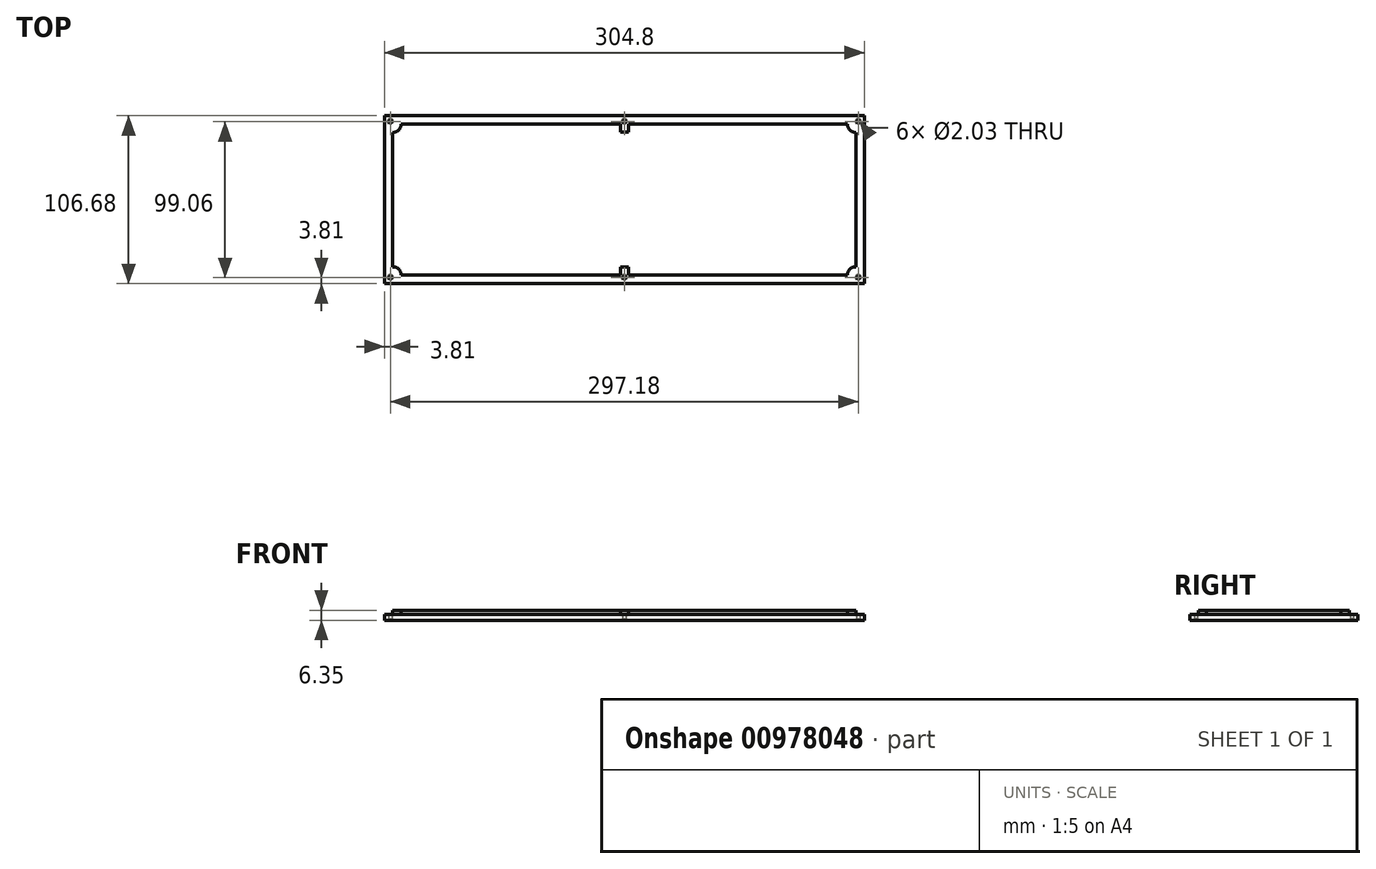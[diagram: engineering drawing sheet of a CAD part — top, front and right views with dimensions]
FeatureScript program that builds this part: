
annotation { "Feature Type Name" : "Feature", "Feature Type Description" : "" }
export const myFeature = defineFeature(function(context is Context, id is Id, definition is map)
    precondition{}
    {
        {
            var Q0;
            Q0=qCreatedBy(makeId("Top.planeOp"),FACE);
            var sketch = newSketch(context, id + "F0", { "sketchPlane" : qUnion([Q0])});
            skLineSegment(sketch, "E0.bottom", {"start": v(0, 0) * mm, "end": v(304.8, 0) * mm});
            skLineSegment(sketch, "E0.top", {"start": v(0, -106.68) * mm, "end": v(304.8, -106.68) * mm});
            skLineSegment(sketch, "E0.left", {"start": v(0, 0) * mm, "end": v(0, -106.68) * mm});
            skLineSegment(sketch, "E0.right", {"start": v(304.8, 0) * mm, "end": v(304.8, -106.68) * mm});
            skSolve(sketch);
        }
        {
            var Q0;
            Q0=makeQuery(id+"F0.imprint","IMPRINT",FACE,{"disambiguationData":[TD([[makeQuery(id+"F0.imprint","IMPRINT",EDGE,{"derivedFrom":sQuery(id+"F0.wireOp",EDGE,"E0.bottom")}),-1.0]])]});
            extrude(context, id + "F1", {"entities" : qUnion([Q0]), "depth" : 3.8 * mm, "offsetDistance" : 25.4 * mm});
        }
        {
            var Q0;
            Q0=makeQuery(id+"F1.opExtrude","CAP_FACE",FACE,{"disambiguationData":[OSD([sQuery(id+"F0.wireOp",EDGE,"E0.bottom"),sQuery(id+"F0.wireOp",EDGE,"E0.top"),sQuery(id+"F0.wireOp",EDGE,"E0.left"),sQuery(id+"F0.wireOp",EDGE,"E0.right")])],"isStart":false});
            var sketch = newSketch(context, id + "F2", { "sketchPlane" : qUnion([Q0])});
            skLineSegment(sketch, "E1.bottom", {"start": v(5.33, -5.33) * mm, "end": v(299.47, -5.33) * mm});
            skLineSegment(sketch, "E1.top", {"start": v(5.33, -101.35) * mm, "end": v(299.47, -101.35) * mm});
            skLineSegment(sketch, "E1.left", {"start": v(5.33, -5.33) * mm, "end": v(5.33, -101.35) * mm});
            skLineSegment(sketch, "E1.right", {"start": v(299.47, -5.33) * mm, "end": v(299.47, -101.35) * mm});
            skSolve(sketch);
        }
        {
            var Q0;
            Q0 = qSketchRegion(id + "F2", true);
            extrude(context, id + "F3", {"entities" : qUnion([Q0]), "operationType" : NewBodyOperationType.ADD, "depth" : 2.54 * mm, "offsetDistance" : 25.4 * mm});
        }
        {
            var Q0;
            Q0=makeQuery(id+"F3.opExtrude","CAP_FACE",FACE,{"disambiguationData":[OSD([sQuery(id+"F2.wireOp",EDGE,"E1.bottom"),sQuery(id+"F2.wireOp",EDGE,"E1.top"),sQuery(id+"F2.wireOp",EDGE,"E1.left"),sQuery(id+"F2.wireOp",EDGE,"E1.right")])],"isStart":false});
            var sketch = newSketch(context, id + "F4", { "sketchPlane" : qUnion([Q0])});
            skLineSegment(sketch, "E2.bottom", {"start": v(5.33, -5.33) * mm, "end": v(10.67, -5.33) * mm});
            skLineSegment(sketch, "E2.top", {"start": v(5.33, -10.67) * mm, "end": v(10.67, -10.67) * mm});
            skLineSegment(sketch, "E2.left", {"start": v(5.33, -5.33) * mm, "end": v(5.33, -10.67) * mm});
            skLineSegment(sketch, "E2.right", {"start": v(10.67, -5.33) * mm, "end": v(10.67, -10.67) * mm});
            skLineSegment(sketch, "E3.bottom", {"start": v(5.33, -101.35) * mm, "end": v(10.67, -101.35) * mm});
            skLineSegment(sketch, "E3.top", {"start": v(5.33, -96.01) * mm, "end": v(10.67, -96.01) * mm});
            skLineSegment(sketch, "E3.left", {"start": v(5.33, -101.35) * mm, "end": v(5.33, -96.01) * mm});
            skLineSegment(sketch, "E3.right", {"start": v(10.67, -101.35) * mm, "end": v(10.67, -96.01) * mm});
            skLineSegment(sketch, "E4.bottom", {"start": v(299.47, -5.33) * mm, "end": v(294.13, -5.33) * mm});
            skLineSegment(sketch, "E4.top", {"start": v(299.47, -10.67) * mm, "end": v(294.13, -10.67) * mm});
            skLineSegment(sketch, "E4.left", {"start": v(299.47, -5.33) * mm, "end": v(299.47, -10.67) * mm});
            skLineSegment(sketch, "E4.right", {"start": v(294.13, -5.33) * mm, "end": v(294.13, -10.67) * mm});
            skLineSegment(sketch, "E5.bottom", {"start": v(299.47, -101.35) * mm, "end": v(294.13, -101.35) * mm});
            skLineSegment(sketch, "E5.top", {"start": v(299.47, -96.01) * mm, "end": v(294.13, -96.01) * mm});
            skLineSegment(sketch, "E5.left", {"start": v(299.47, -101.35) * mm, "end": v(299.47, -96.01) * mm});
            skLineSegment(sketch, "E5.right", {"start": v(294.13, -101.35) * mm, "end": v(294.13, -96.01) * mm});
            skLineSegment(sketch, "E6.bottom", {"start": v(149.86, -5.33) * mm, "end": v(154.94, -5.33) * mm});
            skLineSegment(sketch, "E6.top", {"start": v(149.86, -10.41) * mm, "end": v(154.94, -10.41) * mm});
            skLineSegment(sketch, "E6.left", {"start": v(149.86, -5.33) * mm, "end": v(149.86, -10.41) * mm});
            skLineSegment(sketch, "E6.right", {"start": v(154.94, -5.33) * mm, "end": v(154.94, -10.41) * mm});
            skLineSegment(sketch, "E7.bottom", {"start": v(149.86, -101.35) * mm, "end": v(154.94, -101.35) * mm});
            skLineSegment(sketch, "E7.top", {"start": v(149.86, -96.27) * mm, "end": v(154.94, -96.27) * mm});
            skLineSegment(sketch, "E7.left", {"start": v(149.86, -101.35) * mm, "end": v(149.86, -96.27) * mm});
            skLineSegment(sketch, "E7.right", {"start": v(154.94, -101.35) * mm, "end": v(154.94, -96.27) * mm});
            skSolve(sketch);
        }
        {
            var Q0;
            Q0 = qSketchRegion(id + "F4", true);
            extrude(context, id + "F5", {"entities" : qUnion([Q0]), "operationType" : NewBodyOperationType.ADD, "depth" : 25.4 * mm, "offsetDistance" : 25.4 * mm});
        }
        {
            var Q0;
            Q0=makeQuery(id+"F5.opExtrude","SWEPT_EDGE",EDGE,{"disambiguationData":[OSD([sQuery(id+"F4.wireOp",EDGE,"E5.top"),sQuery(id+"F4.wireOp",EDGE,"E5.right")])]});
            var Q1;
            Q1=makeQuery(id+"F5.opExtrude","SWEPT_EDGE",EDGE,{"disambiguationData":[OSD([sQuery(id+"F4.wireOp",EDGE,"E4.top"),sQuery(id+"F4.wireOp",EDGE,"E4.right")])]});
            var Q2;
            Q2=makeQuery(id+"F5.opExtrude","SWEPT_EDGE",EDGE,{"disambiguationData":[OSD([sQuery(id+"F4.wireOp",EDGE,"E2.top"),sQuery(id+"F4.wireOp",EDGE,"E2.right")])]});
            var Q3;
            Q3=makeQuery(id+"F5.opExtrude","SWEPT_EDGE",EDGE,{"disambiguationData":[OSD([sQuery(id+"F4.wireOp",EDGE,"E3.top"),sQuery(id+"F4.wireOp",EDGE,"E3.right")])]});
            fillet(context, id + "F6", {"entities" : qUnion([Q0, Q1, Q2, Q3]), "tangentPropagation" : true, "radius" : 5.08 * mm, "defaultsChanged" : false, "vertexSettings" : [], "allowEdgeOverflow" : false});
        }
        {
            var Q0;
            Q0=makeQuery(id+"F5.opExtrude","CAP_FACE",FACE,{"disambiguationData":[OSD([sQuery(id+"F4.wireOp",EDGE,"E2.bottom"),sQuery(id+"F4.wireOp",EDGE,"E2.top"),sQuery(id+"F4.wireOp",EDGE,"E2.left"),sQuery(id+"F4.wireOp",EDGE,"E2.right")])],"isStart":false});
            var Q1;
            Q1=makeQuery(id+"F5.opExtrude","CAP_FACE",FACE,{"disambiguationData":[OSD([sQuery(id+"F4.wireOp",EDGE,"E3.bottom"),sQuery(id+"F4.wireOp",EDGE,"E3.top"),sQuery(id+"F4.wireOp",EDGE,"E3.left"),sQuery(id+"F4.wireOp",EDGE,"E3.right")])],"isStart":false});
            var Q2;
            Q2=makeQuery(id+"F5.opExtrude","CAP_FACE",FACE,{"disambiguationData":[OSD([sQuery(id+"F4.wireOp",EDGE,"E4.bottom"),sQuery(id+"F4.wireOp",EDGE,"E4.top"),sQuery(id+"F4.wireOp",EDGE,"E4.left"),sQuery(id+"F4.wireOp",EDGE,"E4.right")])],"isStart":false});
            var Q3;
            Q3=makeQuery(id+"F5.opExtrude","CAP_FACE",FACE,{"disambiguationData":[OSD([sQuery(id+"F4.wireOp",EDGE,"E5.bottom"),sQuery(id+"F4.wireOp",EDGE,"E5.top"),sQuery(id+"F4.wireOp",EDGE,"E5.left"),sQuery(id+"F4.wireOp",EDGE,"E5.right")])],"isStart":false});
            extrude(context, id + "F7", {"entities" : qUnion([Q0, Q1, Q2, Q3]), "operationType" : NewBodyOperationType.REMOVE, "oppositeDirection" : true, "depth" : 27.94 * mm, "offsetDistance" : 25.4 * mm});
        }
        {
            var Q0;
            Q0=makeQuery(id+"F1.opExtrude","CAP_FACE",FACE,{"disambiguationData":[OSD([sQuery(id+"F0.wireOp",EDGE,"E0.bottom"),sQuery(id+"F0.wireOp",EDGE,"E0.top"),sQuery(id+"F0.wireOp",EDGE,"E0.left"),sQuery(id+"F0.wireOp",EDGE,"E0.right")])],"isStart":true});
            var sketch = newSketch(context, id + "F8", { "sketchPlane" : qUnion([Q0])});
            skLineSegment(sketch, "E8.bottom", {"start": v(0, 106.68) * mm, "end": v(3.8, 106.68) * mm});
            skLineSegment(sketch, "E8.top", {"start": v(0, 102.87) * mm, "end": v(3.8, 102.87) * mm});
            skLineSegment(sketch, "E8.left", {"start": v(0, 106.68) * mm, "end": v(0, 102.87) * mm});
            skLineSegment(sketch, "E8.right", {"start": v(3.81, 106.68) * mm, "end": v(3.81, 102.87) * mm});
            skLineSegment(sketch, "E9.bottom", {"start": v(0, 0) * mm, "end": v(3.8, 0) * mm});
            skLineSegment(sketch, "E9.top", {"start": v(0, 3.81) * mm, "end": v(3.8, 3.81) * mm});
            skLineSegment(sketch, "E9.left", {"start": v(0, 0) * mm, "end": v(0, 3.81) * mm});
            skLineSegment(sketch, "E9.right", {"start": v(3.8, 0) * mm, "end": v(3.8, 3.81) * mm});
            skLineSegment(sketch, "E10.bottom", {"start": v(304.8, 106.68) * mm, "end": v(301, 106.68) * mm});
            skLineSegment(sketch, "E10.top", {"start": v(304.8, 102.87) * mm, "end": v(301, 102.87) * mm});
            skLineSegment(sketch, "E10.left", {"start": v(304.8, 106.68) * mm, "end": v(304.8, 102.87) * mm});
            skLineSegment(sketch, "E10.right", {"start": v(301, 106.68) * mm, "end": v(301, 102.87) * mm});
            skLineSegment(sketch, "E11.bottom", {"start": v(304.8, 0) * mm, "end": v(301, 0) * mm});
            skLineSegment(sketch, "E11.top", {"start": v(304.8, 3.81) * mm, "end": v(301, 3.81) * mm});
            skLineSegment(sketch, "E11.left", {"start": v(304.8, 0) * mm, "end": v(304.8, 3.81) * mm});
            skLineSegment(sketch, "E11.right", {"start": v(301, 0) * mm, "end": v(301, 3.81) * mm});
            skLineSegment(sketch, "E12", {"start": v(152.4, 106.68) * mm, "end": v(152.4, 102.87) * mm});
            skLineSegment(sketch, "E13", {"start": v(152.4, 0) * mm, "end": v(152.4, 3.81) * mm});
            skSolve(sketch);
        }
        {
            var Q0;
            Q0=makeQuery(id+"F5.opExtrude","CAP_FACE",FACE,{"disambiguationData":[OSD([sQuery(id+"F4.wireOp",EDGE,"E6.bottom"),sQuery(id+"F4.wireOp",EDGE,"E6.top"),sQuery(id+"F4.wireOp",EDGE,"E6.left"),sQuery(id+"F4.wireOp",EDGE,"E6.right")])],"isStart":false});
            var Q1;
            Q1=makeQuery(id+"F5.opExtrude","CAP_FACE",FACE,{"disambiguationData":[OSD([sQuery(id+"F4.wireOp",EDGE,"E7.bottom"),sQuery(id+"F4.wireOp",EDGE,"E7.top"),sQuery(id+"F4.wireOp",EDGE,"E7.left"),sQuery(id+"F4.wireOp",EDGE,"E7.right")])],"isStart":false});
            extrude(context, id + "F9", {"entities" : qUnion([Q0, Q1]), "operationType" : NewBodyOperationType.REMOVE, "oppositeDirection" : true, "depth" : 27.94 * mm, "offsetDistance" : 25.4 * mm});
        }
        {
            var Q0;
            Q0=sQuery(id+"F8.wireOp",VERTEX,"E8.top.end");
            var Q1;
            Q1=sQuery(id+"F8.wireOp",VERTEX,"E9.top.end");
            var Q2;
            Q2=sQuery(id+"F8.wireOp",VERTEX,"E10.top.end");
            var Q3;
            Q3=sQuery(id+"F8.wireOp",VERTEX,"E11.top.end");
            var Q4;
            Q4=sQuery(id+"F8.wireOp",VERTEX,"E13.end");
            var Q5;
            Q5=sQuery(id+"F8.wireOp",VERTEX,"E12.end");
            var Q6;
            Q6=makeQuery(id+"F1.opExtrude","SWEPT_BODY",BODY,{"disambiguationData":[OSD([sQuery(id+"F0.wireOp",EDGE,"E0.bottom"),sQuery(id+"F0.wireOp",EDGE,"E0.top"),sQuery(id+"F0.wireOp",EDGE,"E0.left"),sQuery(id+"F0.wireOp",EDGE,"E0.right")])]});
            hole(context, id + "F10", {"style" : HoleStyle.C_SINK, "endStyle" : HoleEndStyle.BLIND, "holeDiameter" : 2.03 * mm, "cSinkDiameter" : 3.8 * mm, "cSinkAngle" : 90 * degree, "majorDiameter" : 6.35 * mm, "holeDepth" : 12.7 * mm, "isTappedThrough" : true, "tappedDepth" : 12.7 * mm, "tapClearance" : 3, "locations" : qUnion([Q0, Q1, Q2, Q3, Q4, Q5]), "scope" : qUnion([Q6])});
        }
    });
